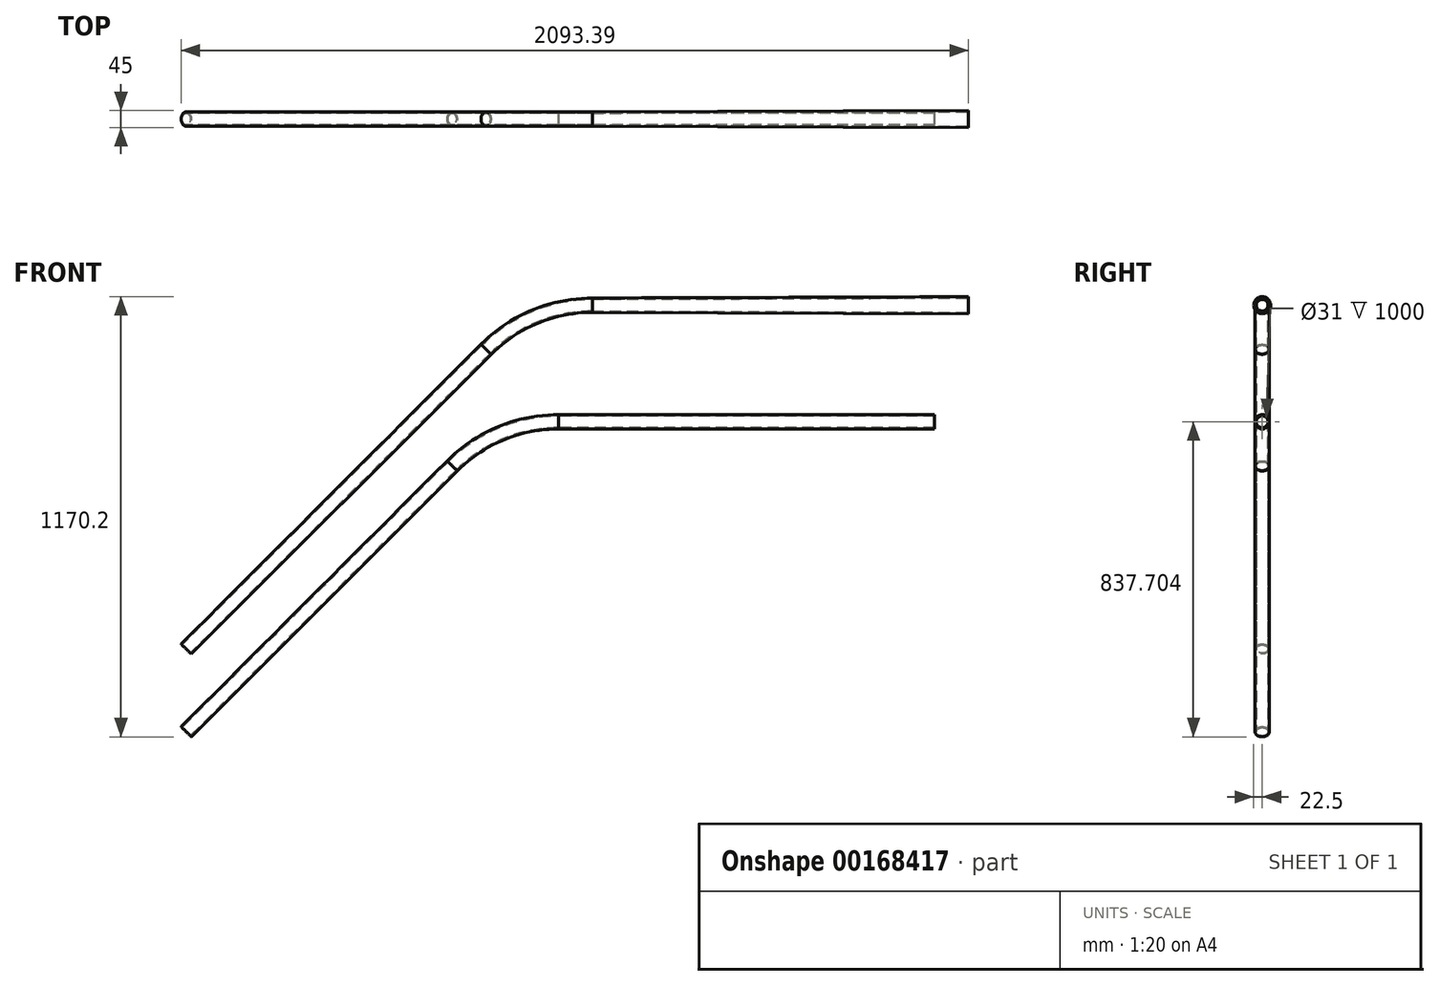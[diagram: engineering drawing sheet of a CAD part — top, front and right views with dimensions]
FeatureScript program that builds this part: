
annotation { "Feature Type Name" : "Feature", "Feature Type Description" : "" }
export const myFeature = defineFeature(function(context is Context, id is Id, definition is map)
    precondition{}
    {
        {
            var Q0;
            Q0=qCreatedBy(makeId("Front.planeOp"),FACE);
            var sketch = newSketch(context, id + "F0", { "sketchPlane" : qUnion([Q0])});
            skLineSegment(sketch, "E0", {"start": v(0, 0) * mm, "end": v(707.1, 707.1) * mm, "construction": true});
            skLineSegment(sketch, "E1", {"start": v(0, 0) * mm, "end": v(0, 220) * mm, "construction": true});
            skLineSegment(sketch, "E2", {"start": v(0, 220) * mm, "end": v(707.1, 927.1) * mm, "construction": true});
            skLineSegment(sketch, "E3", {"start": v(707.1, 927.1) * mm, "end": v(707.1, 707.1) * mm, "construction": true});
            skLineSegment(sketch, "E4", {"start": v(707.1, 927.1) * mm, "end": v(693.67, 940.54) * mm});
            skLineSegment(sketch, "E5", {"start": v(0, 220) * mm, "end": v(-13.44, 233.44) * mm});
            skLineSegment(sketch, "E6", {"start": v(-13.44, 233.44) * mm, "end": v(783.67, 1030.54) * mm});
            skLineSegment(sketch, "E7", {"start": v(786.15, 1028.07) * mm, "end": v(-10.96, 230.96) * mm});
            skLineSegment(sketch, "E8", {"start": v(0, 0) * mm, "end": v(-13.44, 13.44) * mm});
            skLineSegment(sketch, "E9", {"start": v(707.1, 707.1) * mm, "end": v(693.67, 720.54) * mm});
            skLineSegment(sketch, "E10", {"start": v(693.67, 720.54) * mm, "end": v(-13.44, 13.44) * mm});
            skPoint(sketch, "E11", {"position": v(-10.96, 10.96) * mm});
            skPoint(sketch, "E12", {"position": v(696.15, 718.07) * mm});
            skLineSegment(sketch, "E13", {"start": v(696.15, 718.07) * mm, "end": v(-10.96, 10.96) * mm});
            skLineSegment(sketch, "E14", {"start": v(0, 0) * mm, "end": v(707.1, 0) * mm, "construction": true});
            skArc(sketch, "E15", {"start": v(989.95, 824.26) * mm, "mid": v(836.88, 793.82) * mm, "end": v(707.1, 707.1) * mm, "construction": true});
            skLineSegment(sketch, "E16", {"start": v(989.95, 824.26) * mm, "end": v(1989.95, 824.26) * mm, "construction": true});
            skLineSegment(sketch, "E17", {"start": v(707.1, 927.1) * mm, "end": v(797.1, 1017.1) * mm, "construction": true});
            skArc(sketch, "E18", {"start": v(1079.95, 1134.26) * mm, "mid": v(926.88, 1103.82) * mm, "end": v(797.1, 1017.1) * mm, "construction": true});
            skLineSegment(sketch, "E19", {"start": v(1079.95, 1134.26) * mm, "end": v(2079.95, 1134.26) * mm, "construction": true});
            skArc(sketch, "E20.trimOffspring", {"start": v(680.83, 707.7) * mm, "mid": v(681.84, 695.44) * mm, "end": v(683.22, 683.22) * mm, "construction": true});
            skLineSegment(sketch, "E21", {"start": v(797.1, 1017.1) * mm, "end": v(783.67, 1030.54) * mm});
            skArc(sketch, "E22.0", {"start": v(1079.95, 1153.26) * mm, "mid": v(919.6, 1121.37) * mm, "end": v(783.67, 1030.54) * mm});
            skArc(sketch, "E23.0", {"start": v(1079.95, 1149.76) * mm, "mid": v(920.94, 1118.14) * mm, "end": v(786.15, 1028.07) * mm});
            skLineSegment(sketch, "E24", {"start": v(1079.95, 1153.26) * mm, "end": v(1079.95, 1134.26) * mm});
            skLineSegment(sketch, "E25", {"start": v(1079.95, 1149.76) * mm, "end": v(2079.95, 1153.26) * mm});
            skLineSegment(sketch, "E26", {"start": v(1079.95, 1153.26) * mm, "end": v(2079.95, 1156.76) * mm});
            skLineSegment(sketch, "E27", {"start": v(2079.95, 1156.76) * mm, "end": v(2079.95, 1134.26) * mm});
            skArc(sketch, "E28.0", {"start": v(989.95, 843.26) * mm, "mid": v(829.6, 811.37) * mm, "end": v(693.67, 720.54) * mm});
            skArc(sketch, "E29.0", {"start": v(989.95, 839.76) * mm, "mid": v(830.94, 808.14) * mm, "end": v(696.15, 718.07) * mm});
            skLineSegment(sketch, "E30", {"start": v(989.95, 843.26) * mm, "end": v(989.95, 824.26) * mm});
            skLineSegment(sketch, "E31", {"start": v(989.95, 839.76) * mm, "end": v(1989.95, 839.76) * mm});
            skLineSegment(sketch, "E32", {"start": v(989.95, 843.26) * mm, "end": v(1989.95, 843.26) * mm});
            skLineSegment(sketch, "E33", {"start": v(1989.95, 843.26) * mm, "end": v(1989.95, 824.26) * mm});
            skSolve(sketch);
        }
        {
            var Q0;
            {var subQ0=sQuery(id+"F0.wireOp",EDGE,"E6");Q0=makeQuery(id+"F0.imprint","IMPRINT",FACE,{"disambiguationData":[TD([[makeQuery(id+"F0.imprint","IMPRINT",EDGE,{"derivedFrom":subQ0}),-1.0]])]});}
            var Q1;
            Q1=sQuery(id+"F0.wireOp",EDGE,"E2");
            revolve(context, id + "F1", {"entities" : qUnion([Q0]), "axis" : qUnion([Q1]), "revolveType" : RevolveType.FULL});
        }
        {
            var Q0;
            {var subQ0=sQuery(id+"F0.wireOp",EDGE,"E10");Q0=makeQuery(id+"F0.imprint","IMPRINT",FACE,{"disambiguationData":[TD([[makeQuery(id+"F0.imprint","IMPRINT",EDGE,{"derivedFrom":subQ0}),1.0]])]});}
            var Q1;
            Q1=sQuery(id+"F0.wireOp",EDGE,"E0");
            revolve(context, id + "F2", {"entities" : qUnion([Q0]), "axis" : qUnion([Q1]), "revolveType" : RevolveType.FULL});
        }
        {
            var Q0;
            {var subQ2=sQuery(id+"F0.wireOp",EDGE,"E25");Q0=makeQuery(id+"F0.imprint","IMPRINT",FACE,{"disambiguationData":[TD([[makeQuery(id+"F0.imprint","IMPRINT",EDGE,{"derivedFrom":subQ2}),1.0]])]});}
            var Q1;
            Q1=sQuery(id+"F0.wireOp",EDGE,"E19");
            revolve(context, id + "F3", {"entities" : qUnion([Q0]), "axis" : qUnion([Q1]), "revolveType" : RevolveType.FULL});
        }
        {
            var Q0;
            {var subQ2=sQuery(id+"F0.wireOp",EDGE,"E31");Q0=makeQuery(id+"F0.imprint","IMPRINT",FACE,{"disambiguationData":[TD([[makeQuery(id+"F0.imprint","IMPRINT",EDGE,{"derivedFrom":subQ2}),1.0]])]});}
            var Q1;
            Q1=sQuery(id+"F0.wireOp",EDGE,"E16");
            revolve(context, id + "F4", {"entities" : qUnion([Q0]), "axis" : qUnion([Q1]), "revolveType" : RevolveType.FULL});
        }
        {
            var Q0;
            Q0=makeQuery(id+"F1.opRevolve","SWEPT_FACE",FACE,{"disambiguationData":[OSD([sQuery(id+"F0.wireOp",EDGE,"E21")])]});
            var Q1;
            Q1=sQuery(id+"F0.wireOp",EDGE,"E23.0");
            sweep(context, id + "F5", {"profiles" : qUnion([Q0]), "path" : qUnion([Q1])});
        }
        {
            var Q0;
            Q0=makeQuery(id+"F2.opRevolve","SWEPT_FACE",FACE,{"disambiguationData":[OSD([sQuery(id+"F0.wireOp",EDGE,"E9")])]});
            var Q1;
            Q1=sQuery(id+"F0.wireOp",EDGE,"E29.0");
            sweep(context, id + "F6", {"profiles" : qUnion([Q0]), "path" : qUnion([Q1])});
        }
    });
